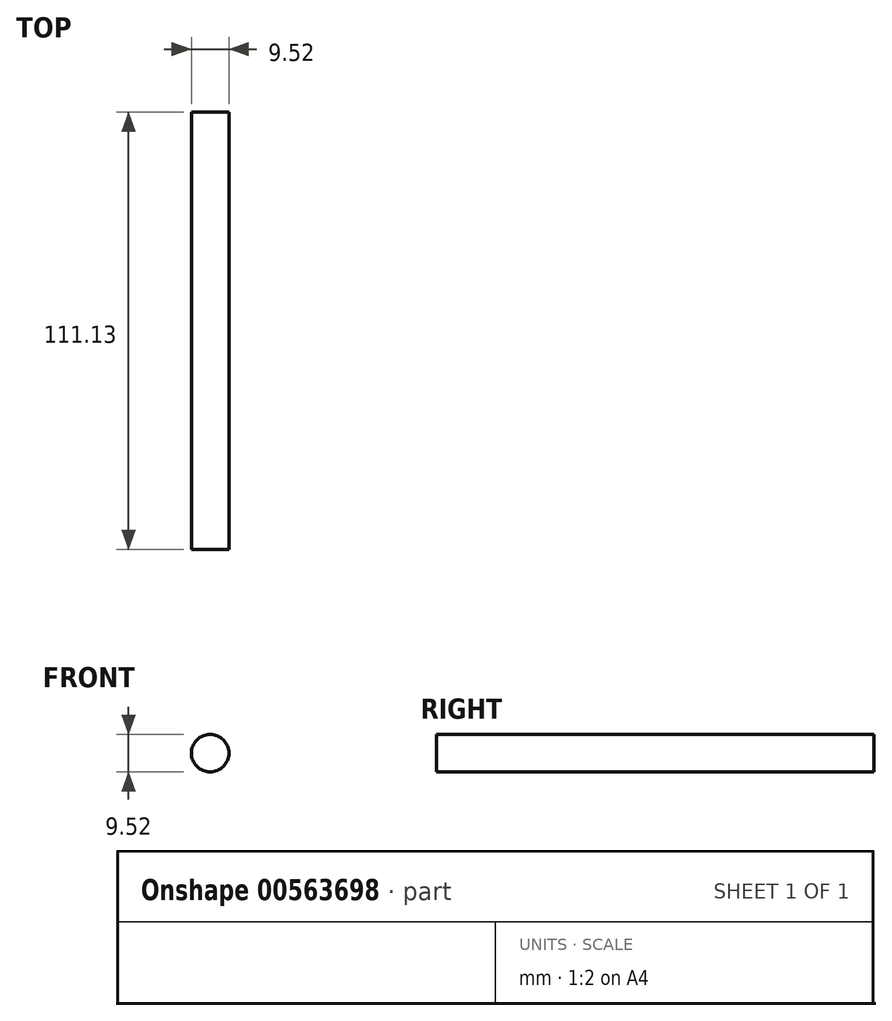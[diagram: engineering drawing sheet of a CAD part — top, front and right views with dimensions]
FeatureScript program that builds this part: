
annotation { "Feature Type Name" : "Feature", "Feature Type Description" : "" }
export const myFeature = defineFeature(function(context is Context, id is Id, definition is map)
    precondition{}
    {
        {
            var Q0;
            Q0=qCreatedBy(makeId("Front.planeOp"),FACE);
            var sketch = newSketch(context, id + "F0", { "sketchPlane" : qUnion([Q0])});
            skCircle(sketch, "E0", {"center": v(0, 0) * mm, "radius": 4.76 * mm});
            skSolve(sketch);
        }
        {
            var Q0;
            Q0 = qSketchRegion(id + "F0", true);
            extrude(context, id + "F1", {"entities" : qUnion([Q0]), "depth" : 111.12 * mm, "offsetDistance" : 25.4 * mm});
        }
    });
